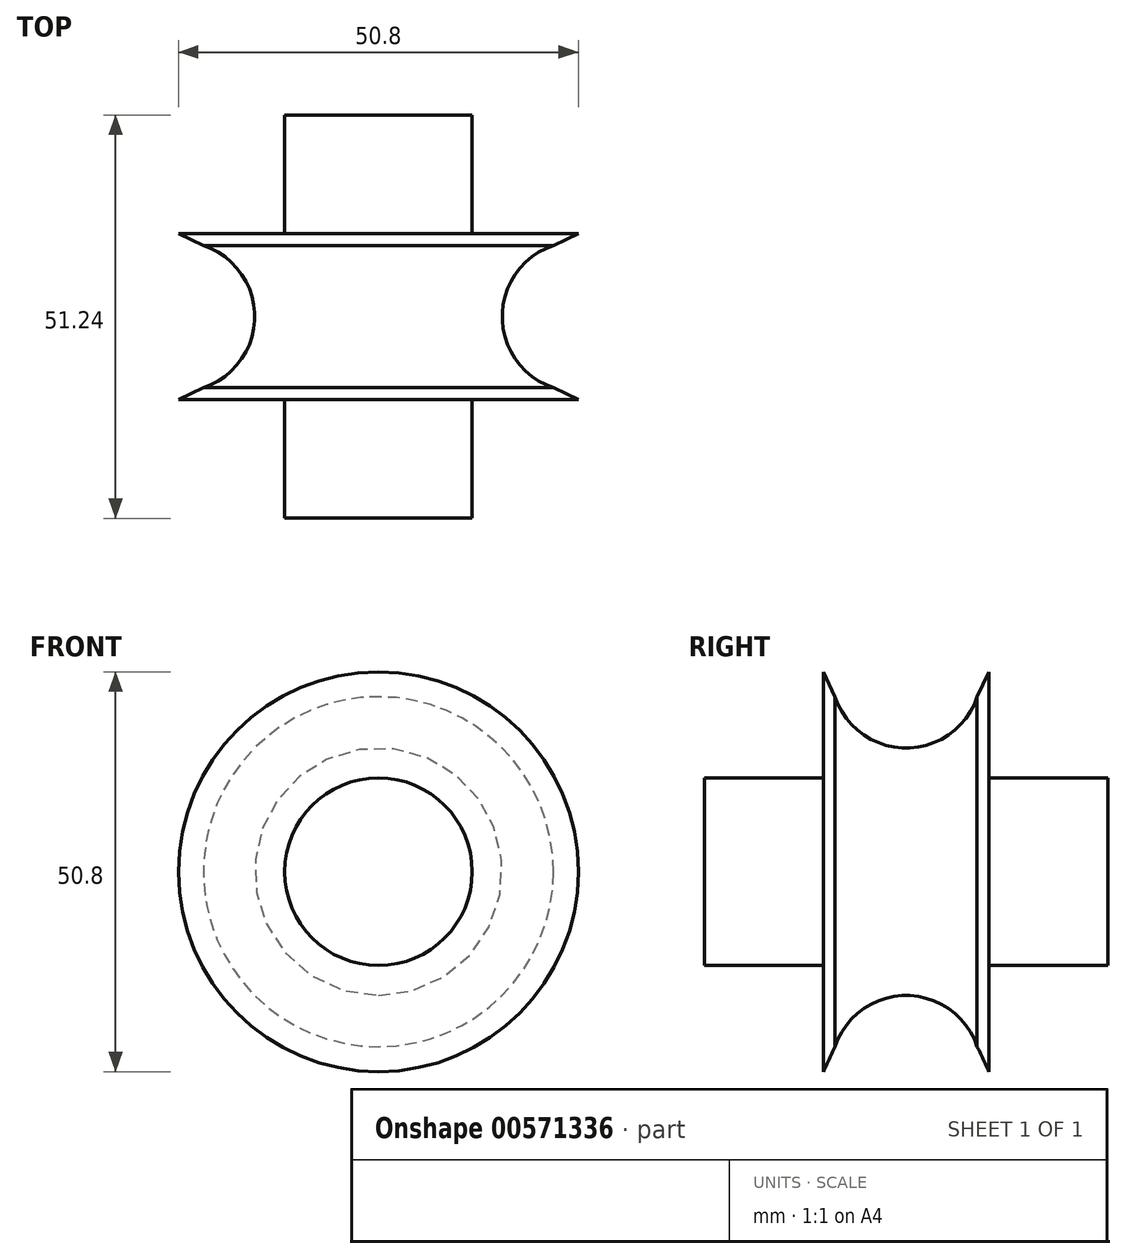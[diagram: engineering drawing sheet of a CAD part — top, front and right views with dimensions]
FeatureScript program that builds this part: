
annotation { "Feature Type Name" : "Feature", "Feature Type Description" : "" }
export const myFeature = defineFeature(function(context is Context, id is Id, definition is map)
    precondition{}
    {
        {
            var Q0;
            Q0=qCreatedBy(makeId("Right.planeOp"),FACE);
            var sketch = newSketch(context, id + "F0", { "sketchPlane" : qUnion([Q0])});
            skLineSegment(sketch, "E0", {"start": v(0, 37) * mm, "end": v(0, -42.8) * mm, "construction": true});
            skLineSegment(sketch, "E1", {"start": v(-25.62, 0) * mm, "end": v(-25.62, 11.91) * mm});
            skLineSegment(sketch, "E2", {"start": v(-25.62, 11.91) * mm, "end": v(-10.52, 11.91) * mm});
            skLineSegment(sketch, "E3", {"start": v(-10.52, 11.91) * mm, "end": v(-10.52, 0) * mm});
            skLineSegment(sketch, "E4", {"start": v(-10.52, 11.91) * mm, "end": v(-10.52, 25.4) * mm});
            skLineSegment(sketch, "E5", {"start": v(-10.52, 25.4) * mm, "end": v(-9.04, 22.22) * mm});
            skLineSegment(sketch, "E6.MirrorCS", {"start": v(10.52, 25.4) * mm, "end": v(9.04, 22.22) * mm});
            skLineSegment(sketch, "E7.MirrorCS", {"start": v(10.52, 11.91) * mm, "end": v(10.52, 25.4) * mm});
            skLineSegment(sketch, "E8.MirrorCS", {"start": v(10.52, 11.91) * mm, "end": v(10.52, 0) * mm});
            skLineSegment(sketch, "E9.MirrorCS", {"start": v(25.62, 11.91) * mm, "end": v(10.52, 11.91) * mm});
            skLineSegment(sketch, "E10.MirrorCS", {"start": v(25.62, 0) * mm, "end": v(25.62, 11.91) * mm});
            skArc(sketch, "E11", {"start": v(-9.04, 22.22) * mm, "mid": v(0, 15.72) * mm, "end": v(9.04, 22.22) * mm});
            skLineSegment(sketch, "E12", {"start": v(-32.56, 0) * mm, "end": v(29.6, 0) * mm, "construction": true});
            skLineSegment(sketch, "E13", {"start": v(-32.56, 0) * mm, "end": v(29.6, 0) * mm});
            skSolve(sketch);
        }
        {
            var Q0;
            Q0 = qSketchRegion(id + "F0", true);
            var Q1;
            Q1=sQuery(id+"F0.wireOp",EDGE,"E13");
            revolve(context, id + "F1", {"entities" : qUnion([Q0]), "axis" : qUnion([Q1]), "revolveType" : RevolveType.FULL});
        }
    });
